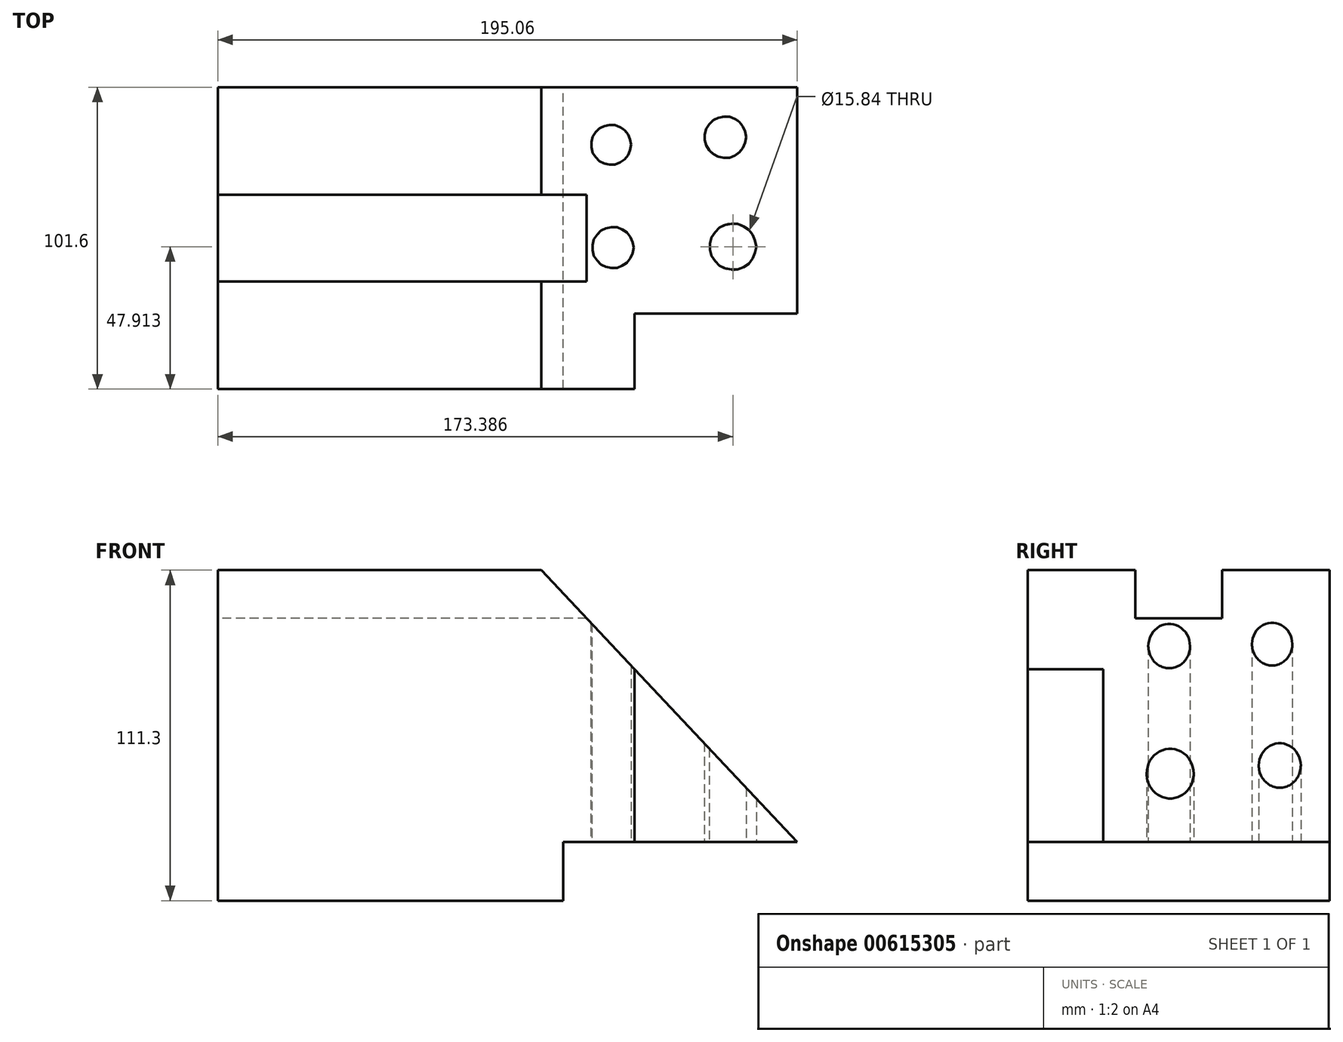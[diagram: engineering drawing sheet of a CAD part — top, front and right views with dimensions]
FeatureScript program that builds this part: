
annotation { "Feature Type Name" : "Feature", "Feature Type Description" : "" }
export const myFeature = defineFeature(function(context is Context, id is Id, definition is map)
    precondition{}
    {
        {
            var Q0;
            Q0=qCreatedBy(makeId("Front.planeOp"),FACE);
            var sketch = newSketch(context, id + "F0", { "sketchPlane" : qUnion([Q0])});
            skLineSegment(sketch, "E0.bottom", {"start": v(-97.53, 55.65) * mm, "end": v(11.37, 55.65) * mm});
            skLineSegment(sketch, "E0.top", {"start": v(-97.53, -55.65) * mm, "end": v(18.74, -55.65) * mm});
            skLineSegment(sketch, "E0.left", {"start": v(-97.53, 55.65) * mm, "end": v(-97.53, -55.65) * mm});
            skPoint(sketch, "E0.middle", {"position": v(0, 0) * mm});
            skLineSegment(sketch, "E1", {"start": v(18.74, -55.65) * mm, "end": v(18.74, -35.87) * mm});
            skLineSegment(sketch, "E2", {"start": v(18.74, -35.87) * mm, "end": v(97.53, -35.87) * mm});
            skLineSegment(sketch, "E3", {"start": v(97.53, -35.87) * mm, "end": v(11.37, 55.65) * mm});
            skPoint(sketch, "E4.orphan", {"position": v(97.53, 55.65) * mm});
            skPoint(sketch, "E0.right.end.orphan", {"position": v(97.53, -55.65) * mm});
            skSolve(sketch);
        }
        {
            var Q0;
            Q0=makeQuery(id+"F0.imprint","IMPRINT",FACE,{"disambiguationData":[TD([[makeQuery(id+"F0.imprint","IMPRINT",EDGE,{"derivedFrom":sQuery(id+"F0.wireOp",EDGE,"E0.bottom")}),-1.0]])]});
            extrude(context, id + "F1", {"entities" : qUnion([Q0]), "endBound" : BoundingType.SYMMETRIC, "depth" : 101.6 * mm, "offsetDistance" : 25.4 * mm});
        }
        {
            var Q0;
            Q0=makeQuery(id+"F1.opExtrude","CAP_FACE",FACE,{"disambiguationData":[OSD([sQuery(id+"F0.wireOp",EDGE,"E0.bottom"),sQuery(id+"F0.wireOp",EDGE,"E0.top"),sQuery(id+"F0.wireOp",EDGE,"E0.left"),sQuery(id+"F0.wireOp",EDGE,"E1"),sQuery(id+"F0.wireOp",EDGE,"E2"),sQuery(id+"F0.wireOp",EDGE,"E3")])],"isStart":false});
            var sketch = newSketch(context, id + "F2", { "sketchPlane" : qUnion([Q0])});
            skLineSegment(sketch, "E5.bottom", {"start": v(42.76, -35.87) * mm, "end": v(98.48, -35.87) * mm});
            skLineSegment(sketch, "E5.top", {"start": v(42.76, 47.08) * mm, "end": v(98.48, 47.08) * mm});
            skLineSegment(sketch, "E5.left", {"start": v(42.76, -35.87) * mm, "end": v(42.76, 47.08) * mm});
            skLineSegment(sketch, "E5.right", {"start": v(98.48, -35.87) * mm, "end": v(98.48, 47.08) * mm});
            skSolve(sketch);
        }
        {
            var Q0;
            Q0 = qSketchRegion(id + "F2", true);
            extrude(context, id + "F3", {"entities" : qUnion([Q0]), "operationType" : NewBodyOperationType.REMOVE, "oppositeDirection" : true, "depth" : 25.4 * mm, "offsetDistance" : 25.4 * mm});
        }
        {
            var Q0;
            Q0=qCreatedBy(makeId("Top.planeOp"),FACE);
            var sketch = newSketch(context, id + "F4", { "sketchPlane" : qUnion([Q0])});
            skCircle(sketch, "E6", {"center": v(34.8, 31.43) * mm, "radius": 6.8 * mm});
            skCircle(sketch, "E7", {"center": v(35.44, -3.2) * mm, "radius": 7.03 * mm});
            skCircle(sketch, "E8", {"center": v(73.29, 34) * mm, "radius": 7.09 * mm});
            skCircle(sketch, "E9", {"center": v(75.86, -2.89) * mm, "radius": 7.92 * mm});
            skSolve(sketch);
        }
        {
            var Q0;
            Q0 = qSketchRegion(id + "F4", true);
            extrude(context, id + "F5", {"entities" : qUnion([Q0]), "operationType" : NewBodyOperationType.REMOVE, "endBound" : BoundingType.SYMMETRIC, "depth" : 127 * mm, "offsetDistance" : 25.4 * mm});
        }
        {
            var Q0;
            Q0=makeQuery(id+"F1.opExtrude","SWEPT_FACE",FACE,{"disambiguationData":[OSD([sQuery(id+"F0.wireOp",EDGE,"E0.left")])]});
            var sketch = newSketch(context, id + "F6", { "sketchPlane" : qUnion([Q0])});
            skLineSegment(sketch, "E10.bottom", {"start": v(-14.65, 39.44) * mm, "end": v(14.65, 39.44) * mm});
            skLineSegment(sketch, "E10.left", {"start": v(-14.65, 39.44) * mm, "end": v(-14.65, 55.65) * mm});
            skLineSegment(sketch, "E10.right", {"start": v(14.65, 39.44) * mm, "end": v(14.65, 55.65) * mm});
            skPoint(sketch, "E10.middle", {"position": v(0, 55.65) * mm});
            skLineSegment(sketch, "E11", {"start": v(-14.65, 55.65) * mm, "end": v(14.65, 55.65) * mm});
            skPoint(sketch, "E10.top.start.orphan", {"position": v(-14.65, 71.86) * mm});
            skPoint(sketch, "E12.orphan", {"position": v(14.65, 71.86) * mm});
            skSolve(sketch);
        }
        {
            var Q0;
            Q0=makeQuery(id+"F6.imprint","IMPRINT",FACE,{"disambiguationData":[TD([[makeQuery(id+"F6.imprint","IMPRINT",EDGE,{"derivedFrom":sQuery(id+"F6.wireOp",EDGE,"E10.bottom")}),1.0]])]});
            extrude(context, id + "F7", {"entities" : qUnion([Q0]), "operationType" : NewBodyOperationType.REMOVE, "oppositeDirection" : true, "depth" : 174.24 * mm, "offsetDistance" : 25.4 * mm});
        }
    });
